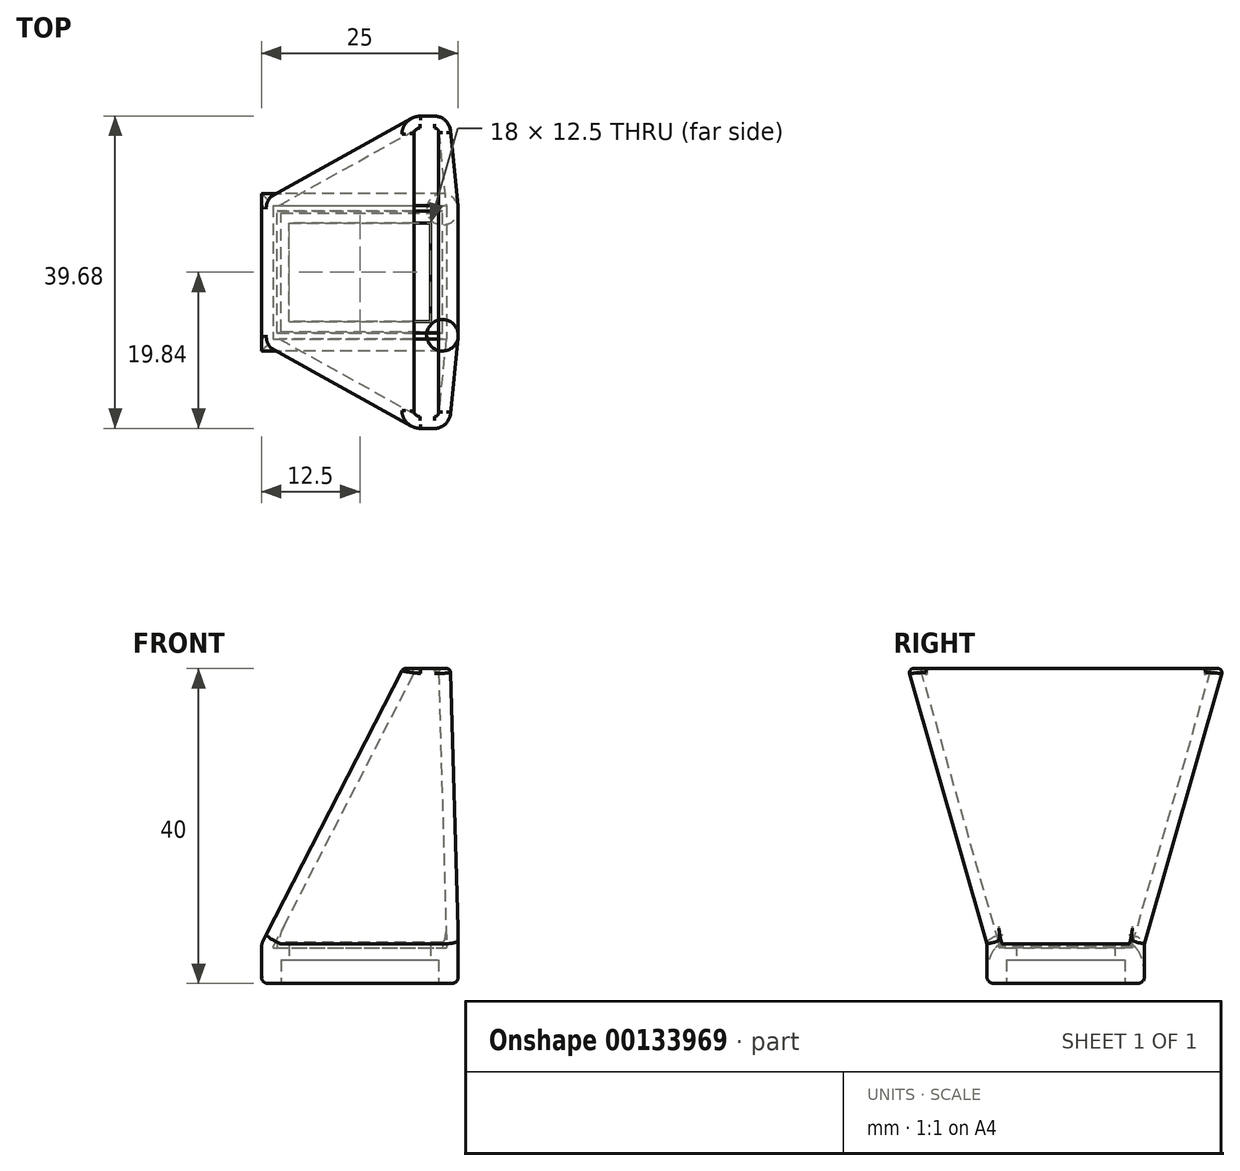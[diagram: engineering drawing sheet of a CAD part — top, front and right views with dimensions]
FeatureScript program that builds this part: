
annotation { "Feature Type Name" : "Feature", "Feature Type Description" : "" }
export const myFeature = defineFeature(function(context is Context, id is Id, definition is map)
    precondition{}
    {
        {
            var Q0;
            Q0=qCreatedBy(makeId("Top.planeOp"),FACE);
            var sketch = newSketch(context, id + "F0", { "sketchPlane" : qUnion([Q0])});
            skLineSegment(sketch, "E0.bottom", {"start": v(12.5, -10) * mm, "end": v(-12.5, -10) * mm});
            skLineSegment(sketch, "E0.top", {"start": v(12.5, 10) * mm, "end": v(-12.5, 10) * mm});
            skLineSegment(sketch, "E0.left", {"start": v(12.5, -10) * mm, "end": v(12.5, 10) * mm});
            skLineSegment(sketch, "E0.right", {"start": v(-12.5, -10) * mm, "end": v(-12.5, 10) * mm});
            skPoint(sketch, "E0.middle", {"position": v(0, 0) * mm});
            skSolve(sketch);
        }
        {
            var Q0;
            Q0 = qSketchRegion(id + "F0", true);
            extrude(context, id + "F1", {"entities" : qUnion([Q0]), "depth" : 5 * mm, "offsetDistance" : 25 * mm});
        }
        {
            var Q0;
            Q0=makeQuery(id+"F1.opExtrude","CAP_FACE",FACE,{"disambiguationData":[OSD([sQuery(id+"F0.wireOp",EDGE,"E0.bottom"),sQuery(id+"F0.wireOp",EDGE,"E0.top"),sQuery(id+"F0.wireOp",EDGE,"E0.left"),sQuery(id+"F0.wireOp",EDGE,"E0.right")])],"isStart":true});
            var sketch = newSketch(context, id + "F2", { "sketchPlane" : qUnion([Q0])});
            skLineSegment(sketch, "E1.bottom", {"start": v(-10, 7.5) * mm, "end": v(10, 7.5) * mm});
            skLineSegment(sketch, "E1.top", {"start": v(-10, -7.5) * mm, "end": v(10, -7.5) * mm});
            skLineSegment(sketch, "E1.left", {"start": v(-10, 7.5) * mm, "end": v(-10, -7.5) * mm});
            skLineSegment(sketch, "E1.right", {"start": v(10, 7.5) * mm, "end": v(10, -7.5) * mm});
            skPoint(sketch, "E1.middle", {"position": v(0, 0) * mm});
            skSolve(sketch);
        }
        {
            var Q0;
            Q0 = qSketchRegion(id + "F2", true);
            extrude(context, id + "F3", {"entities" : qUnion([Q0]), "operationType" : NewBodyOperationType.REMOVE, "oppositeDirection" : true, "depth" : 3 * mm, "offsetDistance" : 25 * mm});
        }
        {
            var Q0;
            Q0=makeQuery(id+"F3.boolean.opBoolean","COPY",FACE,{"derivedFrom":makeQuery(id+"F3.opExtrude","CAP_FACE",FACE,{"disambiguationData":[OSD([sQuery(id+"F2.wireOp",EDGE,"E1.bottom"),sQuery(id+"F2.wireOp",EDGE,"E1.top"),sQuery(id+"F2.wireOp",EDGE,"E1.left"),sQuery(id+"F2.wireOp",EDGE,"E1.right")])],"isStart":false})});
            var sketch = newSketch(context, id + "F4", { "sketchPlane" : qUnion([Q0])});
            skLineSegment(sketch, "E2.bottom", {"start": v(-9, 6.25) * mm, "end": v(9, 6.25) * mm});
            skLineSegment(sketch, "E2.top", {"start": v(-9, -6.25) * mm, "end": v(9, -6.25) * mm});
            skLineSegment(sketch, "E2.left", {"start": v(-9, 6.25) * mm, "end": v(-9, -6.25) * mm});
            skLineSegment(sketch, "E2.right", {"start": v(9, 6.25) * mm, "end": v(9, -6.25) * mm});
            skPoint(sketch, "E2.middle", {"position": v(0, 0) * mm});
            skSolve(sketch);
        }
        {
            var Q0;
            Q0 = qSketchRegion(id + "F4", true);
            extrude(context, id + "F5", {"entities" : qUnion([Q0]), "operationType" : NewBodyOperationType.REMOVE, "endBound" : BoundingType.THROUGH_ALL, "oppositeDirection" : true, "depth" : 25 * mm, "offsetDistance" : 25 * mm});
        }
        {
            var Q0;
            Q0=qCreatedBy(makeId("Top.planeOp"),FACE);
            cPlane(context, id + "F6", {"entities" : qUnion([Q0]), "cplaneType" : CPlaneType.OFFSET, "offset" : 40 * mm, "width" : 150 * mm, "height" : 150 * mm});
        }
        {
            var Q0;
            Q0=qCreatedBy(id+"F6.planeOp",FACE);
            var sketch = newSketch(context, id + "F7", { "sketchPlane" : qUnion([Q0])});
            skLineSegment(sketch, "E3.bottom", {"start": v(11.5, 20) * mm, "end": v(5.5, 20) * mm});
            skLineSegment(sketch, "E3.top", {"start": v(11.5, -20) * mm, "end": v(5.5, -20) * mm});
            skLineSegment(sketch, "E3.left", {"start": v(11.5, 20) * mm, "end": v(11.5, -20) * mm});
            skLineSegment(sketch, "E3.right", {"start": v(5.5, 20) * mm, "end": v(5.5, -20) * mm});
            skPoint(sketch, "E3.middle", {"position": v(8.5, 0) * mm});
            skSolve(sketch);
        }
        {
            var Q0;
            Q0=makeQuery(id+"F1.opExtrude","CAP_FACE",FACE,{"disambiguationData":[OSD([sQuery(id+"F0.wireOp",EDGE,"E0.bottom"),sQuery(id+"F0.wireOp",EDGE,"E0.top"),sQuery(id+"F0.wireOp",EDGE,"E0.left"),sQuery(id+"F0.wireOp",EDGE,"E0.right")])],"isStart":false});
            var sketch = newSketch(context, id + "F8", { "sketchPlane" : qUnion([Q0])});
            skLineSegment(sketch, "E4.0", {"start": v(-12.5, -10) * mm, "end": v(-12.5, 10) * mm});
            skLineSegment(sketch, "E4.1", {"start": v(12.5, 10) * mm, "end": v(-12.5, 10) * mm});
            skLineSegment(sketch, "E4.2", {"start": v(12.5, -10) * mm, "end": v(12.5, 10) * mm});
            skLineSegment(sketch, "E4.3", {"start": v(12.5, -10) * mm, "end": v(-12.5, -10) * mm});
            skSolve(sketch);
        }
        {
            var Q1;
            Q1 = qSketchRegion(id + "F7", true);
            var Q2;
            Q2 = qSketchRegion(id + "F8", true);
            loft(context, id + "F9", {"operationType" : NewBodyOperationType.ADD, "sheetProfilesArray" : [{ "sheetProfileEntities" : qUnion([Q1]) }, { "sheetProfileEntities" : qUnion([Q2]) }]});
        }
        {
            var Q0;
            Q0=makeQuery(id+"F9.opLoft","CAP_FACE",FACE,{"disambiguationData":[OSD([makeQuery(id+"F7.imprint","IMPRINT",FACE,{"disambiguationData":[TD([[makeQuery(id+"F7.imprint","IMPRINT",EDGE,{"derivedFrom":sQuery(id+"F7.wireOp",EDGE,"E3.bottom")}),1.0]])]})])],"isStart":true});
            var Q1;
            {var subQ0=makeQuery(id+"F1.opExtrude","CAP_FACE",FACE,{"disambiguationData":[OSD([sQuery(id+"F0.wireOp",EDGE,"E0.bottom"),sQuery(id+"F0.wireOp",EDGE,"E0.top"),sQuery(id+"F0.wireOp",EDGE,"E0.left"),sQuery(id+"F0.wireOp",EDGE,"E0.right")])],"isStart":false});Q1=makeQuery(id+"F9.opLoft","CAP_FACE",FACE,{"disambiguationData":[OSD([makeQuery(id+"F8.imprint","IMPRINT",FACE,{"disambiguationData":[TD([[makeQuery(id+"F8.imprint","IMPRINT",EDGE,{"derivedFrom":makeQuery(id+"F5.boolean.opBoolean","INTERSECT",EDGE,{"derivedFrom":[subQ0,makeQuery(id+"F5.opExtrude","SWEPT_FACE",FACE,{"disambiguationData":[OSD([sQuery(id+"F4.wireOp",EDGE,"E2.bottom")])]})]})}),-1.0]])]})])],"isStart":true});}
            shell(context, id + "F10", {"entities" : qUnion([Q0, Q1]), "thickness" : 1.5 * mm});
        }
        {
            var Q0;
            Q0=makeQuery(id+"F9.opLoft","SWEPT_EDGE",EDGE,{"disambiguationData":[OSD([sQuery(id+"F7.wireOp",EDGE,"E3.top"),sQuery(id+"F7.wireOp",EDGE,"E3.right"),sQuery(id+"F8.wireOp",EDGE,"E4.0"),sQuery(id+"F8.wireOp",EDGE,"E4.3")])]});
            var Q1;
            Q1=makeQuery(id+"F9.opLoft","SWEPT_EDGE",EDGE,{"disambiguationData":[OSD([sQuery(id+"F7.wireOp",EDGE,"E3.top"),sQuery(id+"F7.wireOp",EDGE,"E3.left"),sQuery(id+"F8.wireOp",EDGE,"E4.2"),sQuery(id+"F8.wireOp",EDGE,"E4.3")])]});
            var Q2;
            Q2=makeQuery(id+"F9.opLoft","SWEPT_EDGE",EDGE,{"disambiguationData":[OSD([sQuery(id+"F7.wireOp",EDGE,"E3.bottom"),sQuery(id+"F7.wireOp",EDGE,"E3.right"),sQuery(id+"F8.wireOp",EDGE,"E4.0"),sQuery(id+"F8.wireOp",EDGE,"E4.1")])]});
            var Q3;
            Q3=makeQuery(id+"F9.opLoft","SWEPT_EDGE",EDGE,{"disambiguationData":[OSD([sQuery(id+"F7.wireOp",EDGE,"E3.bottom"),sQuery(id+"F7.wireOp",EDGE,"E3.left"),sQuery(id+"F8.wireOp",EDGE,"E4.1"),sQuery(id+"F8.wireOp",EDGE,"E4.2")])]});
            fillet(context, id + "F11", {"entities" : qUnion([Q0, Q1, Q2, Q3]), "radius" : 2 * mm, "tangentPropagation" : true, "allowEdgeOverflow" : false});
        }
        {
            var Q0;
            Q0=makeQuery(id+"F11.opFillet","TWEAK_EDGE",EDGE,{"derivedFrom":[makeQuery(id+"F9.boolean.opBoolean","MERGE",VERTEX,{"derivedFrom":[makeQuery(id+"F1.opExtrude","CAP_VERTEX",VERTEX,{"disambiguationData":[OSD([sQuery(id+"F0.wireOp",EDGE,"E0.bottom"),sQuery(id+"F0.wireOp",EDGE,"E0.right")])],"isStart":false}),makeQuery(id+"F9.opLoft","MID_CAP_VERTEX",VERTEX,{"disambiguationData":[OSD([sQuery(id+"F8.wireOp",EDGE,"E4.0"),sQuery(id+"F8.wireOp",EDGE,"E4.3")])],"capPos":1.0})]})]});
            var Q1;
            Q1=makeQuery(id+"F9.boolean.opBoolean","MERGE",EDGE,{"derivedFrom":[makeQuery(id+"F1.opExtrude","CAP_EDGE",EDGE,{"disambiguationData":[OSD([sQuery(id+"F0.wireOp",EDGE,"E0.right")])],"isStart":false}),makeQuery(id+"F9.opLoft","MID_CAP_EDGE",EDGE,{"disambiguationData":[OSD([sQuery(id+"F8.wireOp",EDGE,"E4.0"),sQuery(id+"F8.wireOp",EDGE,"E4.1"),sQuery(id+"F8.wireOp",EDGE,"E4.3")])],"capPos":1.0})]});
            var Q2;
            Q2=makeQuery(id+"F11.opFillet","TWEAK_EDGE",EDGE,{"derivedFrom":[makeQuery(id+"F9.boolean.opBoolean","MERGE",VERTEX,{"derivedFrom":[makeQuery(id+"F1.opExtrude","CAP_VERTEX",VERTEX,{"disambiguationData":[OSD([sQuery(id+"F0.wireOp",EDGE,"E0.top"),sQuery(id+"F0.wireOp",EDGE,"E0.right")])],"isStart":false}),makeQuery(id+"F9.opLoft","MID_CAP_VERTEX",VERTEX,{"disambiguationData":[OSD([sQuery(id+"F8.wireOp",EDGE,"E4.0"),sQuery(id+"F8.wireOp",EDGE,"E4.1")])],"capPos":1.0})]})]});
            var Q3;
            Q3=makeQuery(id+"F1.opExtrude","SWEPT_EDGE",EDGE,{"disambiguationData":[OSD([sQuery(id+"F0.wireOp",EDGE,"E0.top"),sQuery(id+"F0.wireOp",EDGE,"E0.left")])]});
            var Q4;
            Q4=makeQuery(id+"F1.opExtrude","SWEPT_EDGE",EDGE,{"disambiguationData":[OSD([sQuery(id+"F0.wireOp",EDGE,"E0.bottom"),sQuery(id+"F0.wireOp",EDGE,"E0.left")])]});
            fillet(context, id + "F12", {"entities" : qUnion([Q0, Q1, Q2, Q3, Q4]), "radius" : 2 * mm, "tangentPropagation" : true, "allowEdgeOverflow" : false});
        }
        {
            var Q0;
            Q0=makeQuery(id+"F10.opShell","OFFSET_EDGE",EDGE,{"disambiguationData":[OSD([sQuery(id+"F7.wireOp",EDGE,"E3.bottom"),sQuery(id+"F7.wireOp",EDGE,"E3.right"),sQuery(id+"F8.wireOp",EDGE,"E4.0"),sQuery(id+"F8.wireOp",EDGE,"E4.1")])]});
            var Q1;
            Q1=makeQuery(id+"F10.opShell","OFFSET_EDGE",EDGE,{"disambiguationData":[OSD([sQuery(id+"F7.wireOp",EDGE,"E3.bottom"),sQuery(id+"F7.wireOp",EDGE,"E3.left"),sQuery(id+"F8.wireOp",EDGE,"E4.1"),sQuery(id+"F8.wireOp",EDGE,"E4.2")])]});
            var Q2;
            Q2=makeQuery(id+"F10.opShell","OFFSET_EDGE",EDGE,{"disambiguationData":[OSD([sQuery(id+"F7.wireOp",EDGE,"E3.top"),sQuery(id+"F7.wireOp",EDGE,"E3.left"),sQuery(id+"F8.wireOp",EDGE,"E4.2"),sQuery(id+"F8.wireOp",EDGE,"E4.3")])]});
            var Q3;
            Q3=makeQuery(id+"F10.opShell","OFFSET_EDGE",EDGE,{"disambiguationData":[OSD([sQuery(id+"F7.wireOp",EDGE,"E3.top"),sQuery(id+"F7.wireOp",EDGE,"E3.right"),sQuery(id+"F8.wireOp",EDGE,"E4.0"),sQuery(id+"F8.wireOp",EDGE,"E4.3")])]});
            fillet(context, id + "F13", {"entities" : qUnion([Q0, Q1, Q2, Q3]), "radius" : 0.5 * mm, "tangentPropagation" : true, "allowEdgeOverflow" : false});
        }
        {
            var Q0;
            Q0=makeQuery(id+"F9.opLoft","CAP_FACE",FACE,{"disambiguationData":[OSD([makeQuery(id+"F7.imprint","IMPRINT",FACE,{"disambiguationData":[TD([[makeQuery(id+"F7.imprint","IMPRINT",EDGE,{"derivedFrom":sQuery(id+"F7.wireOp",EDGE,"E3.bottom")}),1.0]])]})])],"isStart":true});
            fillet(context, id + "F14", {"entities" : qUnion([Q0]), "radius" : 0.5 * mm, "tangentPropagation" : true, "allowEdgeOverflow" : false});
        }
        {
            var Q0;
            Q0=makeQuery(id+"F1.opExtrude","CAP_EDGE",EDGE,{"disambiguationData":[OSD([sQuery(id+"F0.wireOp",EDGE,"E0.right")])],"isStart":true});
            var Q1;
            Q1=makeQuery(id+"F1.opExtrude","CAP_EDGE",EDGE,{"disambiguationData":[OSD([sQuery(id+"F0.wireOp",EDGE,"E0.bottom")])],"isStart":true});
            var Q2;
            {var subQ0=sQuery(id+"F0.wireOp",EDGE,"E0.left");var subQ1=sQuery(id+"F0.wireOp",EDGE,"E0.bottom");Q2=makeQuery(id+"F12.opFillet","BLEND_EDGE",EDGE,{"blendedFrom":[makeQuery(id+"F1.opExtrude","SWEPT_EDGE",EDGE,{"disambiguationData":[OSD([subQ1,subQ0])]}),makeQuery(id+"F1.opExtrude","CAP_FACE",FACE,{"disambiguationData":[OSD([subQ1,sQuery(id+"F0.wireOp",EDGE,"E0.top"),subQ0,sQuery(id+"F0.wireOp",EDGE,"E0.right")])],"isStart":true})],"blendedInto":[makeQuery(id+"F1.opExtrude","CAP_FACE",FACE,{"disambiguationData":[OSD([subQ1,sQuery(id+"F0.wireOp",EDGE,"E0.top"),subQ0,sQuery(id+"F0.wireOp",EDGE,"E0.right")])],"isStart":true})]});}
            var Q3;
            Q3=makeQuery(id+"F1.opExtrude","CAP_EDGE",EDGE,{"disambiguationData":[OSD([sQuery(id+"F0.wireOp",EDGE,"E0.left")])],"isStart":true});
            var Q4;
            {var subQ0=sQuery(id+"F0.wireOp",EDGE,"E0.left");var subQ1=sQuery(id+"F0.wireOp",EDGE,"E0.top");Q4=makeQuery(id+"F12.opFillet","BLEND_EDGE",EDGE,{"blendedFrom":[makeQuery(id+"F1.opExtrude","SWEPT_EDGE",EDGE,{"disambiguationData":[OSD([subQ1,subQ0])]}),makeQuery(id+"F1.opExtrude","CAP_FACE",FACE,{"disambiguationData":[OSD([sQuery(id+"F0.wireOp",EDGE,"E0.bottom"),subQ1,subQ0,sQuery(id+"F0.wireOp",EDGE,"E0.right")])],"isStart":true})],"blendedInto":[makeQuery(id+"F1.opExtrude","CAP_FACE",FACE,{"disambiguationData":[OSD([sQuery(id+"F0.wireOp",EDGE,"E0.bottom"),subQ1,subQ0,sQuery(id+"F0.wireOp",EDGE,"E0.right")])],"isStart":true})]});}
            var Q5;
            Q5=makeQuery(id+"F1.opExtrude","CAP_EDGE",EDGE,{"disambiguationData":[OSD([sQuery(id+"F0.wireOp",EDGE,"E0.top")])],"isStart":true});
            fillet(context, id + "F15", {"entities" : qUnion([Q0, Q1, Q2, Q3, Q4, Q5]), "radius" : 0.8 * mm, "tangentPropagation" : true, "allowEdgeOverflow" : false});
        }
    });
